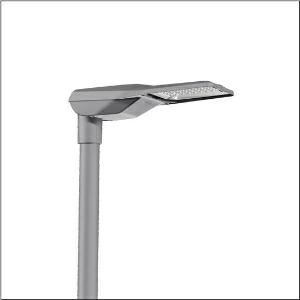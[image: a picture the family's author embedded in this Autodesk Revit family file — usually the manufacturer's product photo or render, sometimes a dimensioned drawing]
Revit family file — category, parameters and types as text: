
# Revit family: streetlight_sl_21_iq_mini___stw1_0a_5xe2e41d08jb_35ba
name_source: partatom
category: Lighting Fixtures
units: mm (PartAtom-declared; Revit-internal decimal feet)

## family parameters
Cut with Voids When Loaded = No
Host = Face
Light Source = No
Part Type = Normal
Room Calculation Point = No
Round Connector Dimension = Use Diameter
Shared = No

## types (1)
- --- (1 x LED, 11290 lm, 71.6 W, 4000K)
    Apparent Load = 72 VA
    CIE Flux Codes = 39 75 98 100 100
    Color Rendering = 70
    Color Temperature = 4000K
    Default Elevation = 1800 mm
    Description = Streetlight SL 21 iQ mini, mast luminaire, primary light control with lens, of PMMA, primary optical cover: cover, of toughened safety glass, transparent, light distribution: STW1.0a, light emission: direct distribution, primary light characteristic: asymmetric, installation type: post-top, side-entry, LED, High Power LED, rated luminous flux: 11.290lm, luminous efficacy: 158lm/W, light colour: 740, colour temperature: 4000K, control: Auto-Match, Temp-Guard, Lumen-Switch, Night-Set, Smart-Wire, Light-Fading, Desk-Remote (wireless, voltage-free reading and setting of iQ features in the workshop via application-optimized NFC function/RFID function), optimised constant luminous flux control (CLO 2.0), presetting dimming linear, mains connection: 220..240V, AC, 50/60Hz, start of lifetime: 72W, end of service life: 75W, reduction: 33W, luminaire housing, of diecast aluminium, powder-coated, Siteco® metallic grey (DB 702S), corrosivity category C5 mid according to DIN EN ISO 12944, please order mast flange separately, inclination adjustable: 0°, 5°, 10°, 15°, sealing non-destructively replaceable, multi-level sealing system, length: 628mm, width: 235mm, height: 110mm, mast flange for spigot size: 42mm (side-entry): 5XC10008XM4, 60/48mm (side-entry/post-top): 5XC10108XM2, 76/60mm (side-entry/post-top): 5XC10108XM1, protection rating (complete): IP66, insulation class (complete): insulation class II (safety insulation), certification: CE, ENEC, ENEC+, VDE, impact resistance: IK09, permissible operating ambient temperature for outdoor applications: -40..+50°C, standard-compliant lighting for roads and squares, packaging unit: 1 piece

Light Distribution: STW1.0a
    Height = 110 mm
    Lamp = 1 x LED
    Lamp Light Flux = 11290 lm
    Lamp Power = 71.6 W
    Lamp count = 1
    Length = 625 mm
    Luminous efficacy = 158 lm/W
    Manufacturer = Siteco
    ModVariant = No
    Model = 5XE2E41D08JB
    Number of Poles = 1
    OnlyDefault = Yes
    Power Factor = 1
    Product Name = Streetlight SL 21 iQ mini | STW1.0a
    Product group = mast luminaire | pylon top
    ProductGroupID = 6100
    Protection Class = Protection class II
    Protection Degree = IP 66
    RLX_Detail_Level = 1
    RLX_Emergency_Light_Flux = 0 lm
    RLX_Emergency_Type = 0
    RLX_Emergency_Type_DB = No
    RlxData = <blob elided: 92421 chars, md5=e2e5443c>
    Socket = socket
    Standby Power = 0 W
    System Light Flux = 11290 lm
    System Power = 72 W
    Type Comments = factory setting: luminous flux: 100 % | dim-lin: 254 | 746 mA
    Type Image = l_1003519.jpg
    URL = http://relux.com
    VarID = @adj_102891
    Voltage = 0 V
    Weight = 0.00 kg
    Width = 234 mm

## geometry (parser evidence)
native form markers: Blend x4, Sweep x11
no freeform markers — native parametric forms only
